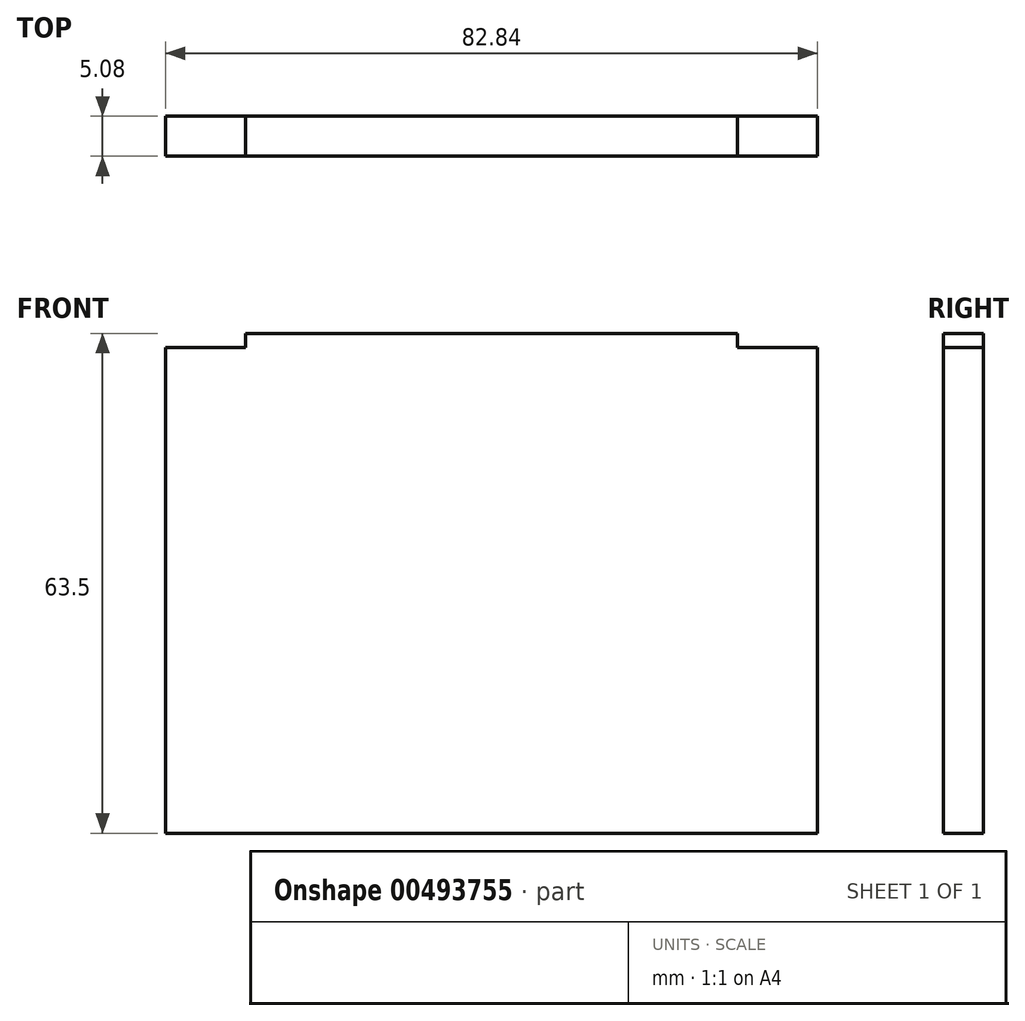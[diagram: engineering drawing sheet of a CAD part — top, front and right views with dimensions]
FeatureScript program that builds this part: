
annotation { "Feature Type Name" : "Feature", "Feature Type Description" : "" }
export const myFeature = defineFeature(function(context is Context, id is Id, definition is map)
    precondition{}
    {
        {
            var Q0;
            Q0=qCreatedBy(makeId("Front.planeOp"),FACE);
            var sketch = newSketch(context, id + "F0", { "sketchPlane" : qUnion([Q0])});
            skLineSegment(sketch, "E0.bottom", {"start": v(-30.21, 1.78) * mm, "end": v(32.27, 1.78) * mm});
            skLineSegment(sketch, "E0.top", {"start": v(-40.4, -61.72) * mm, "end": v(42.43, -61.72) * mm});
            skLineSegment(sketch, "E0.left", {"start": v(-40.4, 0) * mm, "end": v(-40.4, -61.72) * mm});
            skLineSegment(sketch, "E0.right", {"start": v(42.43, 0) * mm, "end": v(42.43, -61.72) * mm});
            skLineSegment(sketch, "E1.top", {"start": v(-40.4, 0) * mm, "end": v(-30.21, 0) * mm});
            skLineSegment(sketch, "E1.right", {"start": v(-30.21, 1.78) * mm, "end": v(-30.21, 0) * mm});
            skLineSegment(sketch, "E2.top", {"start": v(42.43, 0) * mm, "end": v(32.27, 0) * mm});
            skLineSegment(sketch, "E2.right", {"start": v(32.27, 1.78) * mm, "end": v(32.27, 0) * mm});
            skSolve(sketch);
        }
        {
            var Q0;
            Q0=makeQuery(id+"F0.imprint","IMPRINT",FACE,{"disambiguationData":[TD([[makeQuery(id+"F0.imprint","IMPRINT",EDGE,{"derivedFrom":sQuery(id+"F0.wireOp",EDGE,"E0.bottom")}),-1.0]])]});
            extrude(context, id + "F1", {"entities" : qUnion([Q0]), "depth" : 5.08 * mm});
        }
    });
